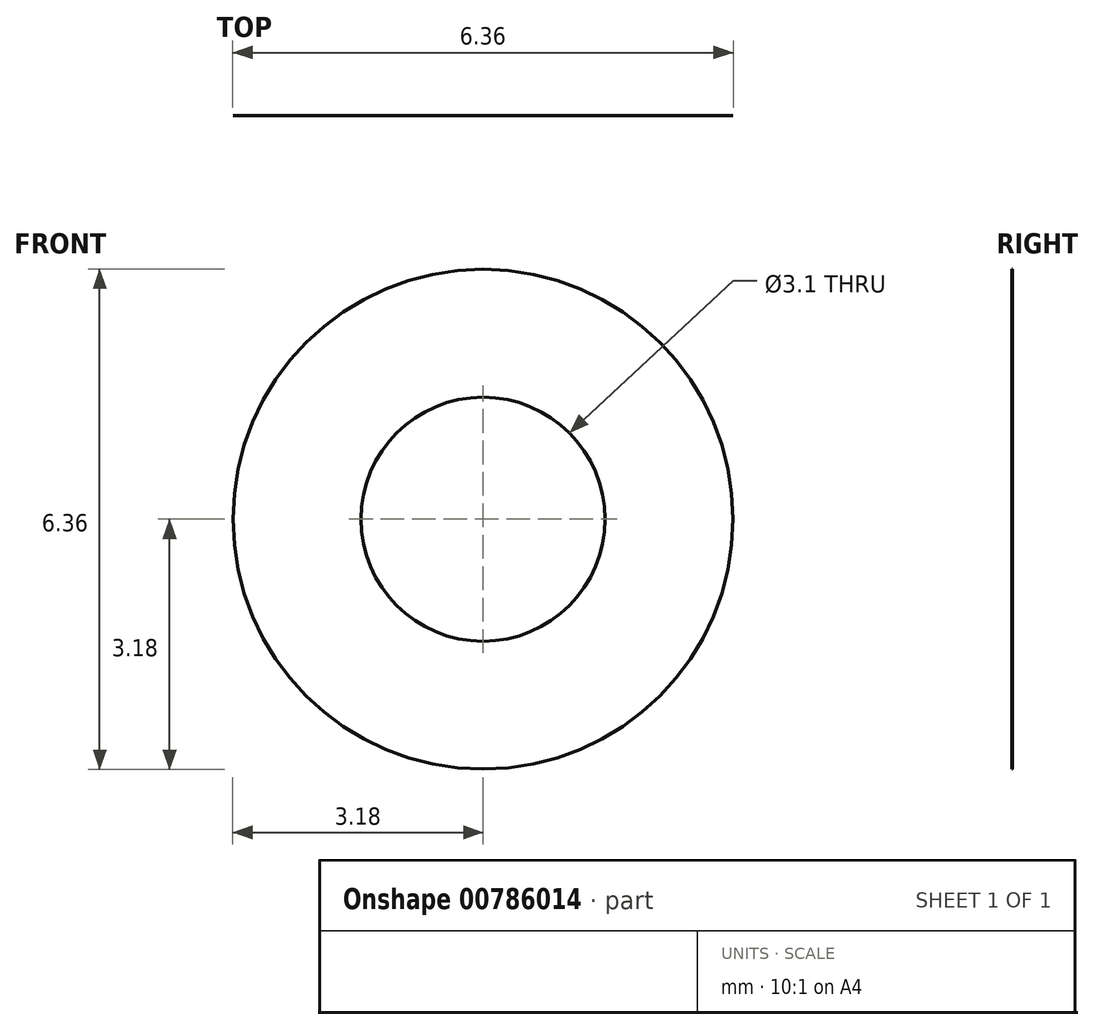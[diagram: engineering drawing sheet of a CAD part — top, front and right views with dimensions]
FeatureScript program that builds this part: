
annotation { "Feature Type Name" : "Feature", "Feature Type Description" : "" }
export const myFeature = defineFeature(function(context is Context, id is Id, definition is map)
    precondition{}
    {
        {
            var Q0;
            Q0=qCreatedBy(makeId("Front.planeOp"),FACE);
            var sketch = newSketch(context, id + "F0", { "sketchPlane" : qUnion([Q0])});
            skCircle(sketch, "E0", {"center": v(0, 0) * mm, "radius": 1.55 * mm});
            skCircle(sketch, "E1", {"center": v(0, 0) * mm, "radius": 3.18 * mm});
            skSolve(sketch);
        }
        {
            var Q0;
            Q0=qSketchRegion(id+"F0",true);
            extrude(context, id + "F1", {"entities" : qUnion([Q0]), "depth" : 1 / 203.2 * mm, "offsetDistance" : 25 * mm});
        }
    });
